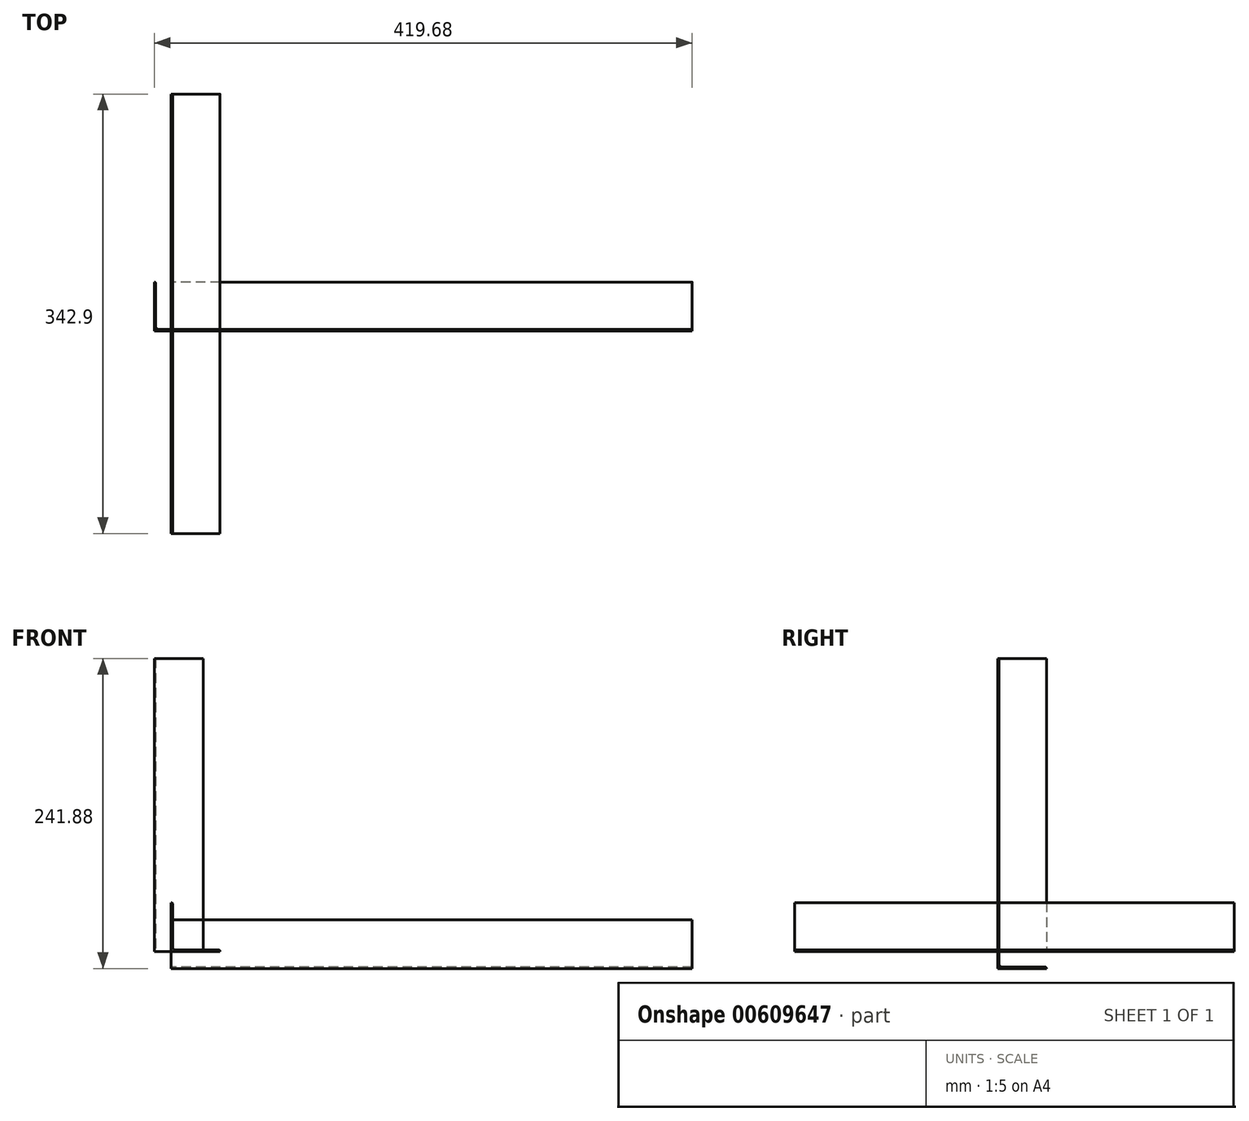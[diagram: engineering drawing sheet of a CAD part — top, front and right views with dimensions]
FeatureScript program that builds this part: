
annotation { "Feature Type Name" : "Feature", "Feature Type Description" : "" }
export const myFeature = defineFeature(function(context is Context, id is Id, definition is map)
    precondition{}
    {
        {
            var Q0;
            Q0=qCreatedBy(makeId("Front.planeOp"),FACE);
            var sketch = newSketch(context, id + "F0", { "sketchPlane" : qUnion([Q0])});
            skLineSegment(sketch, "E0", {"start": v(0, 38.1) * mm, "end": v(0, 0) * mm});
            skLineSegment(sketch, "E1", {"start": v(0, 0) * mm, "end": v(38.1, 0) * mm});
            skLineSegment(sketch, "E2.0", {"start": v(3.5, 1.14) * mm, "end": v(36.96, 1.14) * mm});
            skLineSegment(sketch, "E3.0", {"start": v(1.14, 36.96) * mm, "end": v(1.14, 3.5) * mm});
            skLineSegment(sketch, "E4", {"start": v(0, 38.1) * mm, "end": v(0, 38.1) * mm});
            skLineSegment(sketch, "E5", {"start": v(38.1, 0) * mm, "end": v(38.1, 0) * mm});
            skPoint(sketch, "E6.visualSharp", {"position": v(1.14, 1.14) * mm});
            skArc(sketch, "E6.filletArc", {"start": v(1.14, 3.5) * mm, "mid": v(1.83, 1.83) * mm, "end": v(3.5, 1.14) * mm});
            skPoint(sketch, "E7.visualSharp", {"position": v(1.14, 38.1) * mm});
            skArc(sketch, "E7.filletArc", {"start": v(1.14, 36.96) * mm, "mid": v(0.8, 37.77) * mm, "end": v(0, 38.1) * mm});
            skPoint(sketch, "E8.visualSharp", {"position": v(38.1, 1.14) * mm});
            skArc(sketch, "E8.filletArc", {"start": v(38.1, 0) * mm, "mid": v(37.77, 0.8) * mm, "end": v(36.96, 1.14) * mm});
            skSolve(sketch);
        }
        {
            var Q0;
            Q0=makeQuery(id+"F0.imprint","IMPRINT",FACE,{"disambiguationData":[TD([[makeQuery(id+"F0.imprint","IMPRINT",EDGE,{"derivedFrom":sQuery(id+"F0.wireOp",EDGE,"E0")}),1.0]])]});
            extrude(context, id + "F1", {"entities" : qUnion([Q0]), "depth" : 342.9 * mm, "offsetDistance" : 25.4 * mm, "symmetric" : true});
        }
        {
            var Q0;
            Q0=qCreatedBy(makeId("Top.planeOp"),FACE);
            var sketch = newSketch(context, id + "F2", { "sketchPlane" : qUnion([Q0])});
            skLineSegment(sketch, "E9", {"start": v(-13.28, 24.82) * mm, "end": v(-13.28, -13.28) * mm});
            skLineSegment(sketch, "E10", {"start": v(-13.28, -13.28) * mm, "end": v(24.82, -13.28) * mm});
            skLineSegment(sketch, "E11.0", {"start": v(-9.77, -12.13) * mm, "end": v(23.68, -12.13) * mm});
            skLineSegment(sketch, "E12.0", {"start": v(-12.13, 23.68) * mm, "end": v(-12.13, -9.77) * mm});
            skLineSegment(sketch, "E13", {"start": v(-13.28, 24.82) * mm, "end": v(-13.28, 24.82) * mm});
            skLineSegment(sketch, "E14", {"start": v(24.82, -13.28) * mm, "end": v(24.82, -13.28) * mm});
            skPoint(sketch, "E15.visualSharp", {"position": v(-12.13, -12.13) * mm});
            skArc(sketch, "E15.filletArc", {"start": v(-12.13, -9.77) * mm, "mid": v(-11.44, -11.44) * mm, "end": v(-9.77, -12.13) * mm});
            skPoint(sketch, "E16.visualSharp", {"position": v(-12.13, 24.82) * mm});
            skArc(sketch, "E16.filletArc", {"start": v(-12.13, 23.68) * mm, "mid": v(-12.47, 24.49) * mm, "end": v(-13.28, 24.82) * mm});
            skPoint(sketch, "E17.visualSharp", {"position": v(24.82, -12.13) * mm});
            skArc(sketch, "E17.filletArc", {"start": v(24.82, -13.28) * mm, "mid": v(24.49, -12.47) * mm, "end": v(23.68, -12.13) * mm});
            skSolve(sketch);
        }
        {
            var Q0;
            Q0=makeQuery(id+"F2.imprint","IMPRINT",FACE,{"disambiguationData":[TD([[makeQuery(id+"F2.imprint","IMPRINT",EDGE,{"derivedFrom":sQuery(id+"F2.wireOp",EDGE,"E9")}),1.0]])]});
            extrude(context, id + "F3", {"entities" : qUnion([Q0]), "depth" : 228.6 * mm, "offsetDistance" : 25.4 * mm});
        }
        {
            var Q0;
            Q0=qCreatedBy(makeId("Right.planeOp"),FACE);
            var sketch = newSketch(context, id + "F4", { "sketchPlane" : qUnion([Q0])});
            skLineSegment(sketch, "E18", {"start": v(-13.28, 24.82) * mm, "end": v(-13.28, -13.28) * mm});
            skLineSegment(sketch, "E19", {"start": v(-13.28, -13.28) * mm, "end": v(24.82, -13.28) * mm});
            skLineSegment(sketch, "E20.0", {"start": v(-9.77, -12.13) * mm, "end": v(23.68, -12.13) * mm});
            skLineSegment(sketch, "E21.0", {"start": v(-12.13, 23.68) * mm, "end": v(-12.13, -9.77) * mm});
            skLineSegment(sketch, "E22", {"start": v(-13.28, 24.82) * mm, "end": v(-13.28, 24.82) * mm});
            skLineSegment(sketch, "E23", {"start": v(24.82, -13.28) * mm, "end": v(24.82, -13.28) * mm});
            skPoint(sketch, "E24.visualSharp", {"position": v(-12.13, -12.13) * mm});
            skArc(sketch, "E24.filletArc", {"start": v(-12.13, -9.77) * mm, "mid": v(-11.44, -11.44) * mm, "end": v(-9.77, -12.13) * mm});
            skPoint(sketch, "E25.visualSharp", {"position": v(-12.13, 24.82) * mm});
            skArc(sketch, "E25.filletArc", {"start": v(-12.13, 23.68) * mm, "mid": v(-12.47, 24.49) * mm, "end": v(-13.28, 24.82) * mm});
            skPoint(sketch, "E26.visualSharp", {"position": v(24.82, -12.13) * mm});
            skArc(sketch, "E26.filletArc", {"start": v(24.82, -13.28) * mm, "mid": v(24.49, -12.47) * mm, "end": v(23.68, -12.13) * mm});
            skSolve(sketch);
        }
        {
            var Q0;
            Q0=makeQuery(id+"F4.imprint","IMPRINT",FACE,{"disambiguationData":[TD([[makeQuery(id+"F4.imprint","IMPRINT",EDGE,{"derivedFrom":sQuery(id+"F4.wireOp",EDGE,"E18")}),1.0]])]});
            extrude(context, id + "F5", {"entities" : qUnion([Q0]), "depth" : 406.4 * mm, "offsetDistance" : 25.4 * mm});
        }
    });
